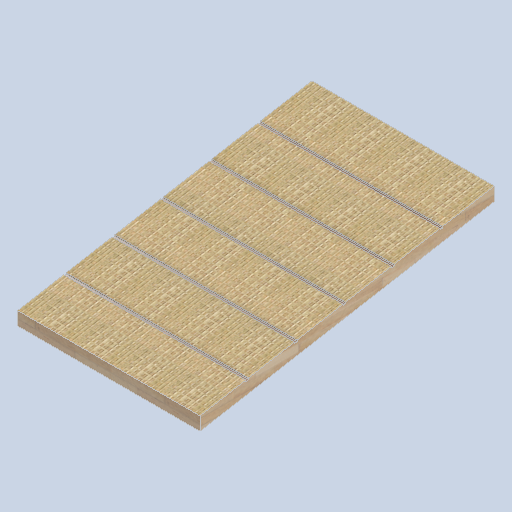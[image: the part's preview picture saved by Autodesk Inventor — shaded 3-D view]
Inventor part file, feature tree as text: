
AUTODESK INVENTOR PART (.ipt)
format: ipt  version: 2024.2 (Build 282272000, 272)  size: 320,512 bytes
history: native  units: in
note: dims shown in document units (in); Inventor stores cm internally (conversion verified against a paired STEP export)
features: sketch x5, other x3, plane x3
ambient origin geometry x8: Origin, YZ Plane, XZ Plane, XY Plane, X Axis, Y Axis, Z Axis, Center Point
bodies: Solid1 (feature_tree)
feature tree (11):
  other  "eave_panel_01_MIR.ipt"
  other  "Solid1::eave_panel_01_MIR.ipt"
  other  "TaggingFeature1"
  sketch  "Sketch1"  dims[d0=0.3937in]
  sketch  "Sketch2"
  sketch  "Sketch3"
  sketch  "Sketch4"
  sketch  "Sketch5"
  plane  "Work Plane1"
  plane  "Work Plane2"
  plane  "Work Plane3"
